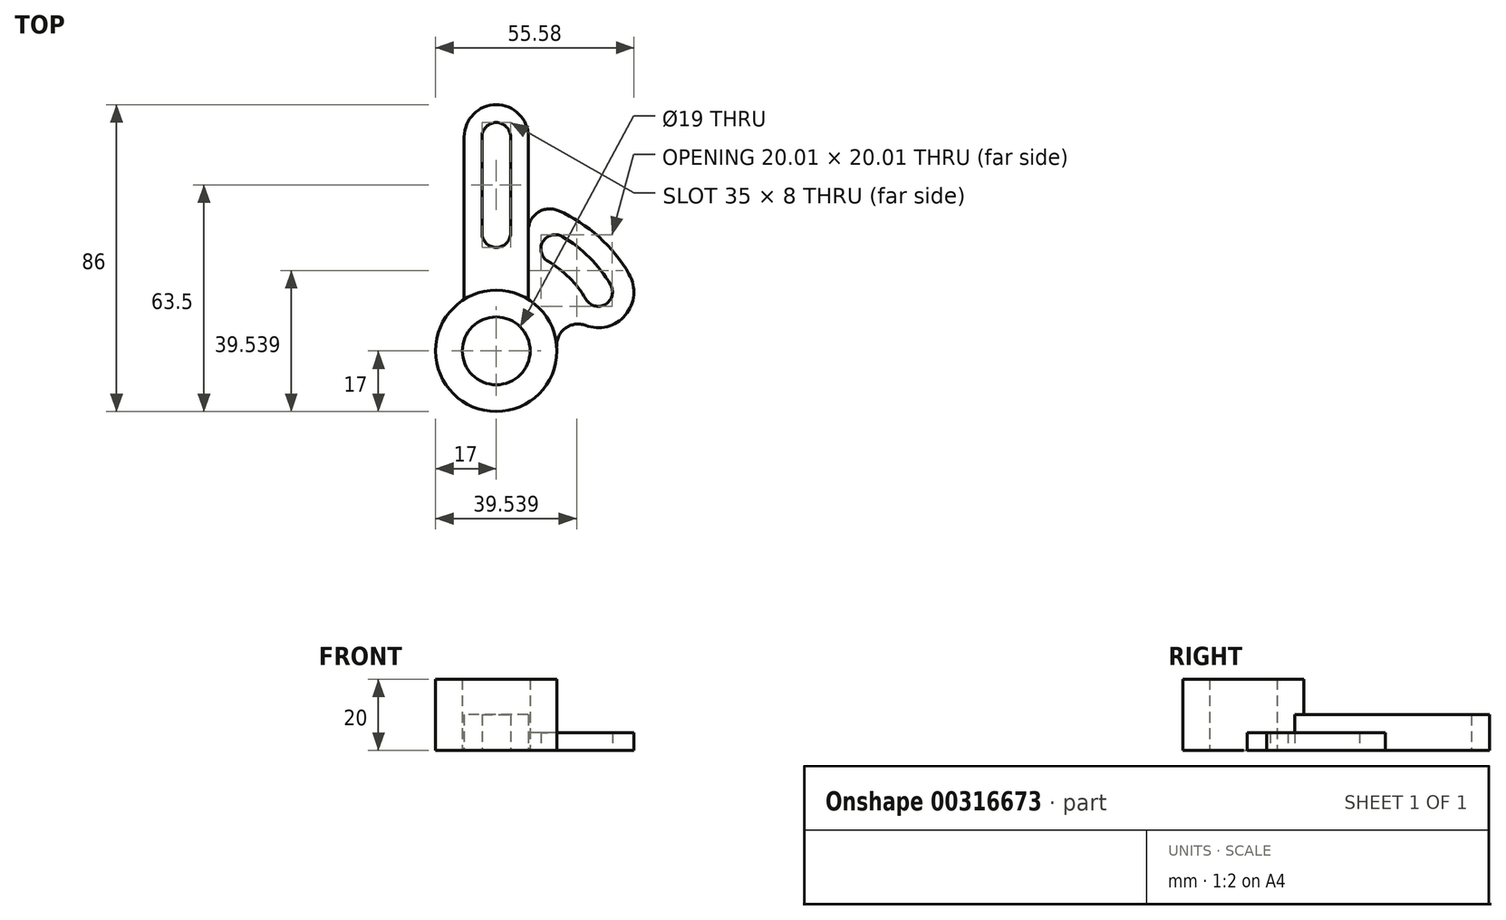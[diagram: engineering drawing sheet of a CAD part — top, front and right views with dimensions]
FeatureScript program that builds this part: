
annotation { "Feature Type Name" : "Feature", "Feature Type Description" : "" }
export const myFeature = defineFeature(function(context is Context, id is Id, definition is map)
    precondition{}
    {
        {
            var Q0;
            Q0=qCreatedBy(makeId("Top.planeOp"),FACE);
            var sketch = newSketch(context, id + "F0", { "sketchPlane" : qUnion([Q0])});
            skCircle(sketch, "E0", {"center": v(0, 0) * mm, "radius": 17 * mm});
            skCircle(sketch, "E1", {"center": v(0, 0) * mm, "radius": 9.5 * mm});
            skArc(sketch, "E2", {"start": v(9, 60) * mm, "mid": v(0, 69) * mm, "end": v(-9, 60) * mm});
            skArc(sketch, "E3", {"start": v(4, 60) * mm, "mid": v(0, 64) * mm, "end": v(-4, 60) * mm});
            skLineSegment(sketch, "E4", {"start": v(-9, 60) * mm, "end": v(-9, 14.42) * mm});
            skLineSegment(sketch, "E5.MirrorCS", {"start": v(9, 60) * mm, "end": v(9, 14.42) * mm});
            skArc(sketch, "E6", {"start": v(-4, 33) * mm, "mid": v(0, 29) * mm, "end": v(4, 33) * mm});
            skLineSegment(sketch, "E7", {"start": v(-4, 60) * mm, "end": v(-4, 33) * mm});
            skLineSegment(sketch, "E8", {"start": v(4, 33) * mm, "end": v(4, 60) * mm});
            skCircle(sketch, "E9", {"center": v(0, 0) * mm, "radius": 43 * mm});
            skLineSegment(sketch, "E10", {"start": v(0, 0) * mm, "end": v(37.24, 21.5) * mm, "construction": true});
            skLineSegment(sketch, "E11", {"start": v(0, 0) * mm, "end": v(21.5, 37.24) * mm, "construction": true});
            skArc(sketch, "E12", {"start": v(28.58, 16.5) * mm, "mid": v(23.33, 23.33) * mm, "end": v(16.5, 28.58) * mm, "construction": true});
            skArc(sketch, "E13", {"start": v(25.06, 7.14) * mm, "mid": v(19.37, 6.34) * mm, "end": v(16.96, 1.13) * mm});
            skArc(sketch, "E14.trimOffspring", {"start": v(25.06, 7.14) * mm, "mid": v(36.2, 10.03) * mm, "end": v(37.24, 21.5) * mm});
            skArc(sketch, "E15", {"start": v(25.11, 14.5) * mm, "mid": v(30.58, 13.04) * mm, "end": v(32.04, 18.5) * mm});
            skArc(sketch, "E16", {"start": v(18.5, 32.04) * mm, "mid": v(13.04, 30.58) * mm, "end": v(14.5, 25.11) * mm});
            skArc(sketch, "E17", {"start": v(32.04, 18.5) * mm, "mid": v(26.16, 26.16) * mm, "end": v(18.5, 32.04) * mm});
            skArc(sketch, "E18", {"start": v(25.11, 14.5) * mm, "mid": v(20.5, 20.5) * mm, "end": v(14.5, 25.11) * mm});
            skSolve(sketch);
        }
        {
            var Q0;
            {var subQ1=sQuery(id+"F0.wireOp",EDGE,"E2");Q0=makeQuery(id+"F0.imprint","IMPRINT",FACE,{"disambiguationData":[TD([[makeQuery(id+"F0.imprint","IMPRINT",EDGE,{"derivedFrom":subQ1}),1.0]])]});}
            var Q1;
            {var subQ0=sQuery(id+"F0.wireOp",EDGE,"E6");Q1=makeQuery(id+"F0.imprint","IMPRINT",FACE,{"disambiguationData":[TD([[makeQuery(id+"F0.imprint","IMPRINT",EDGE,{"derivedFrom":subQ0}),-1.0]])]});}
            extrude(context, id + "F1", {"entities" : qUnion([Q0, Q1]), "depth" : 10 * mm});
        }
        {
            var Q0;
            Q0=makeQuery(id+"F0.imprint","IMPRINT",FACE,{"disambiguationData":[TD([[makeQuery(id+"F0.imprint","IMPRINT",EDGE,{"derivedFrom":sQuery(id+"F0.wireOp",EDGE,"E1")}),-1.0]])]});
            extrude(context, id + "F2", {"entities" : qUnion([Q0]), "depth" : 20 * mm});
        }
        {
            var Q0;
            {var subQ5=sQuery(id+"F0.wireOp",EDGE,"E13");Q0=makeQuery(id+"F0.imprint","IMPRINT",FACE,{"disambiguationData":[TD([[makeQuery(id+"F0.imprint","IMPRINT",EDGE,{"derivedFrom":subQ5}),-1.0]])]});}
            extrude(context, id + "F3", {"entities" : qUnion([Q0]), "depth" : 5 * mm});
        }
        {
            var Q0;
            Q0=makeQuery(id+"F3.opExtrude","SWEPT_EDGE",EDGE,{"disambiguationData":[OSD([sQuery(id+"F0.wireOp",EDGE,"E5.MirrorCS"),sQuery(id+"F0.wireOp",EDGE,"E9")])]});
            fillet(context, id + "F4", {"entities" : qUnion([Q0]), "radius" : 6 * mm, "tangentPropagation" : true, "allowEdgeOverflow" : false});
        }
    });
